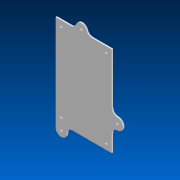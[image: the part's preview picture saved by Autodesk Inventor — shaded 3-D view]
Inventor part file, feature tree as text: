
AUTODESK INVENTOR PART (.ipt)
format: ipt  version: 2022 (Build 260153000, 153)  size: 122,880 bytes
history: native  units: in
note: dims shown in document units (in); Inventor stores cm internally (conversion verified against a paired STEP export)
features: extrude x1, hole x1
ambient origin geometry x8: Origin, YZ Plane, XZ Plane, XY Plane, X Axis, Y Axis, Z Axis, Center Point
bodies: Solid1 (feature_tree)
feature tree (2):
  extrude  "Extrusion1"  Depth=4.0in
  hole  "Hole1"  [1 undecoded]
note: 1 required parameter value undecoded (feature->parameter linkage not recoverable at this tier; creation-order binding heuristic only, values carry confidence <= 0.55)
